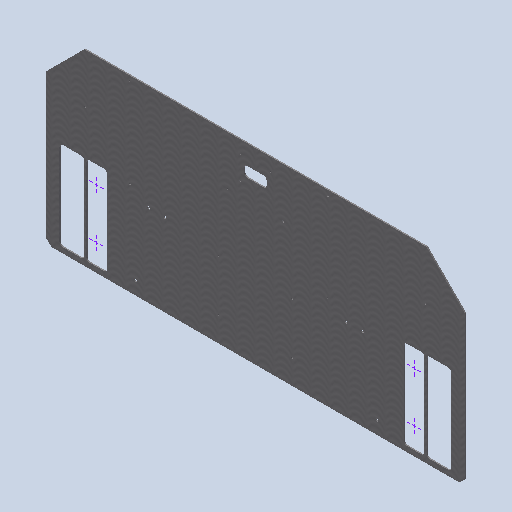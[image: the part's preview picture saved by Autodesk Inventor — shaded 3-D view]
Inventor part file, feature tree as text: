
AUTODESK INVENTOR PART (.ipt)
format: ipt  version: 2022.1 (Build 261234000, 234)  size: 311,296 bytes
history: native  units: mm
features: reference x23, other x20, sketch x7, hole x4, sheet_metal_op x1, chamfer x1
ambient origin geometry x8: Origin, YZ Plane, XZ Plane, XY Plane, X Axis, Y Axis, Z Axis, Center Point
bodies: Solid1 (feature_tree)
feature tree (56):
  sheet_metal_op  "Face1"
  sketch  "Sketch4"  dims[d7=0.0mm d46=74.0mm]
  hole  "Hole1"  [1 undecoded]
  chamfer  "Corner Round2"
  sketch  "Sketch5"  dims[d47=56.0mm]
  hole  "Hole2"  [1 undecoded]
  hole  "Hole3"  [1 undecoded]
  sketch  "Sketch9"  dims[d57=3.0mm]
  hole  "Hole6"  [1 undecoded]
  other  "Plate1"
  sketch  "Sketch2"  dims[d0=3.0mm d6=3.0mm]
  reference  "Referencia11"
  reference  "Referencia12"
  reference  "Reference26"
  reference  "Reference27"
  reference  "Reference28"
  reference  "Reference29"
  reference  "Reference30"
  reference  "Reference31"
  reference  "Reference32"
  reference  "Reference33"
  reference  "Reference34"
  reference  "Reference35"
  reference  "Reference36"
  reference  "Reference37"
  reference  "Reference38"
  reference  "Reference39"
  reference  "Reference40"
  reference  "Reference41"
  reference  "Reference42"
  reference  "Reference43"
  reference  "Reference44"
  sketch  "Sketch6"  dims[d48=3.4mm d49=7.0mm d50=6.3mm d51=2.0mm d52=90.0deg d53=3.0mm d54=20.594885mm]
  sketch  "Sketch7"  dims[d55=54.0mm d56=25.0mm]
  sketch  "Sketch10"  dims[d58=0.0mm d59=60.0mm d60=6.0mm d61=6.6mm d62=6.0mm d63=4.0mm d64=2.0mm d65=90.0deg d66=8.0mm d67=0.0mm d68=4.5mm d69=6.0mm d70=4.0mm d71=2.0mm d72=90.0deg d73=8.0mm d74=0.0mm d89=4.5mm d90=6.0mm d91=4.0mm d92=2.0mm d93=90.0deg d94=8.0mm d95=0.0mm d96=18.0mm d97=205.0mm d98=2.5mm d99=5.0mm d100=5.0mm d101=2.5mm d102=5.0mm d103=2.5mm d104=5.0mm]
  reference  "Referencia45"
  reference  "Referencia46"
  other  "Cut1"
  other  "Cut3"
  other  "<userpath>\Desktop\PDM\ProyectoRobotPallet\RobotPallet.iam"
  other  "RobotPallet.iam"
  other  "BL Motor + Encoder + Gearbox + Rueda:1"
  other  "Rueda:1"
  other  "Exterior_Rueda:1"
  other  "EstructuraInferior - Soldadura:1"
  other  "Frame_Base:1"
  other  "ISO 12633-2 40x40x5 - 2899.41:1"
  other  "Soporte Frontal MotoresMov_Izq:2"
  other  "Soporte_Motor_Encoder:1"
  other  "SKF_SYWK 30 YTH:2"
  other  "housingSYWK 506 Y-h:1"
  other  "BL Motor + Encoder + Gearbox + Rueda:2"
  other  "SKF_SYWK 30 YTH:1"
  other  "Soporte Frontal MotorMovIzq:1"
  other  "ISO 12633-2 40x40x5 - 460:1"
  other  "ISO 12633-2 40x40x5 - 460:2"
note: 4 required parameter values undecoded (feature->parameter linkage not recoverable at this tier; creation-order binding heuristic only, values carry confidence <= 0.55)
